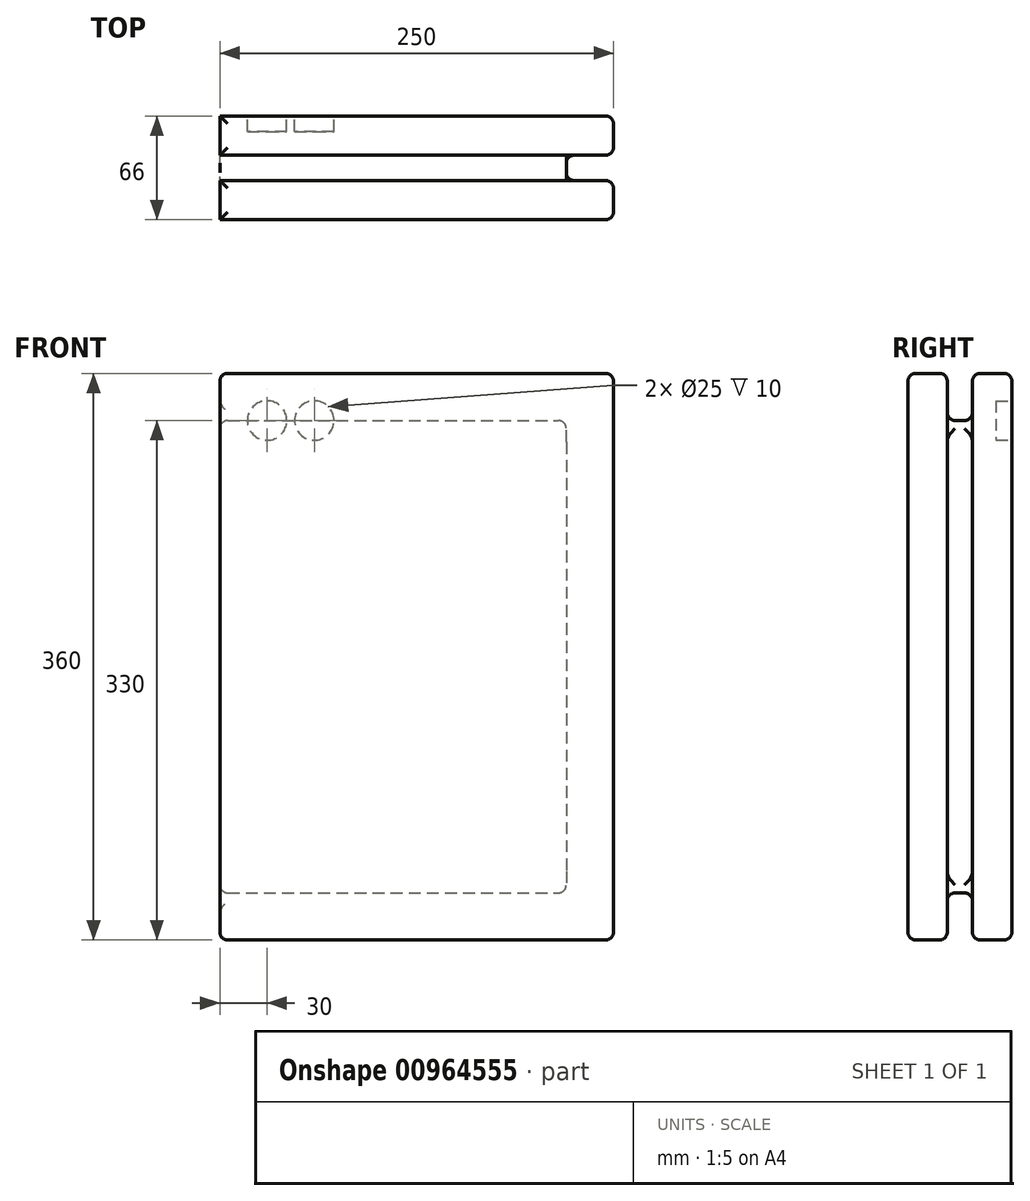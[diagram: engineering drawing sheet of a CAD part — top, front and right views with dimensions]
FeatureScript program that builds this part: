
annotation { "Feature Type Name" : "Feature", "Feature Type Description" : "" }
export const myFeature = defineFeature(function(context is Context, id is Id, definition is map)
    precondition{}
    {
        {
            var Q0;
            Q0=qCreatedBy(makeId("Right.planeOp"),FACE);
            var sketch = newSketch(context, id + "F0", { "sketchPlane" : qUnion([Q0])});
            skLineSegment(sketch, "E0", {"start": v(0, 0) * mm, "end": v(0, 150) * mm, "construction": true});
            skLineSegment(sketch, "E1", {"start": v(0, 0) * mm, "end": v(0, -150) * mm, "construction": true});
            skLineSegment(sketch, "E2", {"start": v(0, 150) * mm, "end": v(8, 150) * mm});
            skLineSegment(sketch, "E3", {"start": v(8, 150) * mm, "end": v(8, 180) * mm});
            skLineSegment(sketch, "E4", {"start": v(8, 180) * mm, "end": v(33, 180) * mm});
            skLineSegment(sketch, "E5", {"start": v(0, 0) * mm, "end": v(80, 0) * mm, "construction": true});
            skLineSegment(sketch, "E6", {"start": v(0, 0) * mm, "end": v(-80, 0) * mm, "construction": true});
            skLineSegment(sketch, "E7.MirrorCS", {"start": v(8, -180) * mm, "end": v(33, -180) * mm});
            skLineSegment(sketch, "E8.MirrorCS", {"start": v(8, -150) * mm, "end": v(8, -180) * mm});
            skLineSegment(sketch, "E9.MirrorCS", {"start": v(0, -150) * mm, "end": v(8, -150) * mm});
            skLineSegment(sketch, "E10", {"start": v(33, 180) * mm, "end": v(33, -180) * mm});
            skLineSegment(sketch, "E11", {"start": v(0, 150) * mm, "end": v(0, -150) * mm, "construction": true});
            skLineSegment(sketch, "E12.MirrorCS", {"start": v(0, 150) * mm, "end": v(-8, 150) * mm});
            skLineSegment(sketch, "E13.MirrorCS", {"start": v(-8, 150) * mm, "end": v(-8, 180) * mm});
            skLineSegment(sketch, "E14.MirrorCS", {"start": v(-8, 180) * mm, "end": v(-33, 180) * mm});
            skLineSegment(sketch, "E15.MirrorCS", {"start": v(-33, 180) * mm, "end": v(-33, -180) * mm});
            skLineSegment(sketch, "E16.MirrorCS", {"start": v(-8, -180) * mm, "end": v(-33, -180) * mm});
            skLineSegment(sketch, "E17.MirrorCS", {"start": v(-8, -150) * mm, "end": v(-8, -180) * mm});
            skLineSegment(sketch, "E18.MirrorCS", {"start": v(0, -150) * mm, "end": v(-8, -150) * mm});
            skSolve(sketch);
        }
        {
            var Q0;
            Q0=qCreatedBy(makeId("Front.planeOp"),FACE);
            var sketch = newSketch(context, id + "F1", { "sketchPlane" : qUnion([Q0])});
            skLineSegment(sketch, "E19", {"start": v(0, 0) * mm, "end": v(250, 0) * mm});
            skSolve(sketch);
        }
        {
            var Q0;
            Q0=qSketchRegion(id+"F0",true);
            var Q1;
            Q1=qConstructionFilter(qBodyType(qCreatedBy(id+"F1",EDGE),BodyType.WIRE),ConstructionObject.NO);
            sweep(context, id + "F2", {"profiles" : qUnion([Q0]), "path" : qUnion([Q1])});
        }
        {
            var Q0;
            Q0=makeQuery(id+"F2.opSweep","SWEPT_FACE",FACE,{"disambiguationData":[OSD([sQuery(id+"F0.wireOp",EDGE,"E10"),sQuery(id+"F1.wireOp",EDGE,"E19")])]});
            var sketch = newSketch(context, id + "F3", { "sketchPlane" : qUnion([Q0])});
            skLineSegment(sketch, "E20", {"start": v(0, 180) * mm, "end": v(-30, 180) * mm, "construction": true});
            skLineSegment(sketch, "E21", {"start": v(-30, 180) * mm, "end": v(-60, 180) * mm, "construction": true});
            skLineSegment(sketch, "E22", {"start": v(-30, 180) * mm, "end": v(-30, 150) * mm, "construction": true});
            skLineSegment(sketch, "E23", {"start": v(-60, 180) * mm, "end": v(-60, 150) * mm, "construction": true});
            skCircle(sketch, "E24", {"center": v(-30, 150) * mm, "radius": 12.5 * mm});
            skCircle(sketch, "E25", {"center": v(-60, 150) * mm, "radius": 12.5 * mm});
            skSolve(sketch);
        }
        {
            var Q0;
            Q0=makeQuery(id+"F3.imprint","IMPRINT",FACE,{"disambiguationData":[TD([[makeQuery(id+"F3.imprint","IMPRINT",EDGE,{"derivedFrom":sQuery(id+"F3.wireOp",EDGE,"E25")}),1.0]])]});
            var Q1;
            Q1=makeQuery(id+"F3.imprint","IMPRINT",FACE,{"disambiguationData":[TD([[makeQuery(id+"F3.imprint","IMPRINT",EDGE,{"derivedFrom":sQuery(id+"F3.wireOp",EDGE,"E24")}),1.0]])]});
            extrude(context, id + "F4", {"entities" : qUnion([Q0, Q1]), "operationType" : NewBodyOperationType.REMOVE, "oppositeDirection" : true, "depth" : 10 * mm, "offsetDistance" : 25 * mm});
        }
        {
            var Q0;
            Q0=makeQuery(id+"F2.opSweep","CAP_FACE",FACE,{"disambiguationData":[OSD([sQuery(id+"F0.wireOp",EDGE,"E2"),sQuery(id+"F0.wireOp",EDGE,"E3"),sQuery(id+"F0.wireOp",EDGE,"E4"),sQuery(id+"F0.wireOp",EDGE,"E7.MirrorCS"),sQuery(id+"F0.wireOp",EDGE,"E8.MirrorCS"),sQuery(id+"F0.wireOp",EDGE,"E9.MirrorCS"),sQuery(id+"F0.wireOp",EDGE,"E10"),sQuery(id+"F0.wireOp",EDGE,"E12.MirrorCS"),sQuery(id+"F0.wireOp",EDGE,"E13.MirrorCS"),sQuery(id+"F0.wireOp",EDGE,"E14.MirrorCS"),sQuery(id+"F0.wireOp",EDGE,"E15.MirrorCS"),sQuery(id+"F0.wireOp",EDGE,"E16.MirrorCS"),sQuery(id+"F0.wireOp",EDGE,"E17.MirrorCS"),sQuery(id+"F0.wireOp",EDGE,"E18.MirrorCS"),sQuery(id+"F1.wireOp",VERTEX,"E19.end")])],"isStart":false});
            var sketch = newSketch(context, id + "F5", { "sketchPlane" : qUnion([Q0])});
            skPoint(sketch, "E26", {"position": v(0, 0) * mm});
            skLineSegment(sketch, "E27", {"start": v(0, 0) * mm, "end": v(0, 150) * mm, "construction": true});
            skLineSegment(sketch, "E28", {"start": v(0, 0) * mm, "end": v(0, -150) * mm, "construction": true});
            skLineSegment(sketch, "E29", {"start": v(0, 150) * mm, "end": v(-8, 150) * mm});
            skLineSegment(sketch, "E30", {"start": v(-8, 150) * mm, "end": v(-8, -150) * mm});
            skLineSegment(sketch, "E31", {"start": v(-8, -150) * mm, "end": v(0, -150) * mm});
            skLineSegment(sketch, "E32.MirrorCS", {"start": v(0, 150) * mm, "end": v(8, 150) * mm});
            skLineSegment(sketch, "E33.MirrorCS", {"start": v(8, 150) * mm, "end": v(8, -150) * mm});
            skLineSegment(sketch, "E34.MirrorCS", {"start": v(8, -150) * mm, "end": v(0, -150) * mm});
            skSolve(sketch);
        }
        {
            var Q0;
            Q0=makeQuery(id+"F5.imprint","IMPRINT",FACE,{"disambiguationData":[TD([[makeQuery(id+"F5.imprint","IMPRINT",EDGE,{"derivedFrom":sQuery(id+"F5.wireOp",EDGE,"E29")}),1.0]])]});
            extrude(context, id + "F6", {"entities" : qUnion([Q0]), "operationType" : NewBodyOperationType.REMOVE, "oppositeDirection" : true, "depth" : 30 * mm, "offsetDistance" : 25 * mm});
        }
        {
            var Q0;
            Q0=makeQuery(id+"F2.opSweep","SWEPT_FACE",FACE,{"disambiguationData":[OSD([sQuery(id+"F0.wireOp",EDGE,"E2"),sQuery(id+"F0.wireOp",EDGE,"E12.MirrorCS"),sQuery(id+"F1.wireOp",EDGE,"E19")])]});
            var Q1;
            Q1=makeQuery(id+"F2.opSweep","SWEPT_FACE",FACE,{"disambiguationData":[OSD([sQuery(id+"F0.wireOp",EDGE,"E9.MirrorCS"),sQuery(id+"F0.wireOp",EDGE,"E18.MirrorCS"),sQuery(id+"F1.wireOp",EDGE,"E19")])]});
            var Q2;
            Q2=makeQuery(id+"F2.opSweep","SWEPT_FACE",FACE,{"disambiguationData":[OSD([sQuery(id+"F0.wireOp",EDGE,"E7.MirrorCS"),sQuery(id+"F1.wireOp",EDGE,"E19")])]});
            var Q3;
            {var subQ1=sQuery(id+"F0.wireOp",EDGE,"E8.MirrorCS");var subQ2=sQuery(id+"F0.wireOp",EDGE,"E7.MirrorCS");var subQ3=sQuery(id+"F0.wireOp",EDGE,"E4");var subQ4=sQuery(id+"F0.wireOp",EDGE,"E3");var subQ5=sQuery(id+"F0.wireOp",EDGE,"E10");Q3=makeQuery(id+"F6.boolean.opBoolean","SPLIT",FACE,{"disambiguationData":[TD([makeQuery(id+"F6.opExtrude","SWEPT_FACE",FACE,{"disambiguationData":[OSD([sQuery(id+"F5.wireOp",EDGE,"E33.MirrorCS")])]})])],"derivedFrom":makeQuery(id+"F2.opSweep","CAP_FACE",FACE,{"disambiguationData":[OSD([sQuery(id+"F0.wireOp",EDGE,"E2"),subQ4,subQ3,subQ2,subQ1,sQuery(id+"F0.wireOp",EDGE,"E9.MirrorCS"),subQ5,sQuery(id+"F0.wireOp",EDGE,"E12.MirrorCS"),sQuery(id+"F0.wireOp",EDGE,"E13.MirrorCS"),sQuery(id+"F0.wireOp",EDGE,"E14.MirrorCS"),sQuery(id+"F0.wireOp",EDGE,"E15.MirrorCS"),sQuery(id+"F0.wireOp",EDGE,"E16.MirrorCS"),sQuery(id+"F0.wireOp",EDGE,"E17.MirrorCS"),sQuery(id+"F0.wireOp",EDGE,"E18.MirrorCS"),sQuery(id+"F1.wireOp",VERTEX,"E19.end")])],"isStart":false})});}
            var Q4;
            Q4=makeQuery(id+"F2.opSweep","SWEPT_FACE",FACE,{"disambiguationData":[OSD([sQuery(id+"F0.wireOp",EDGE,"E4"),sQuery(id+"F1.wireOp",EDGE,"E19")])]});
            var Q5;
            Q5=makeQuery(id+"F2.opSweep","SWEPT_FACE",FACE,{"disambiguationData":[OSD([sQuery(id+"F0.wireOp",EDGE,"E14.MirrorCS"),sQuery(id+"F1.wireOp",EDGE,"E19")])]});
            var Q6;
            {var subQ1=sQuery(id+"F0.wireOp",EDGE,"E16.MirrorCS");var subQ2=sQuery(id+"F0.wireOp",EDGE,"E15.MirrorCS");var subQ3=sQuery(id+"F0.wireOp",EDGE,"E14.MirrorCS");var subQ4=sQuery(id+"F0.wireOp",EDGE,"E13.MirrorCS");var subQ5=sQuery(id+"F0.wireOp",EDGE,"E17.MirrorCS");Q6=makeQuery(id+"F6.boolean.opBoolean","SPLIT",FACE,{"disambiguationData":[TD([makeQuery(id+"F6.opExtrude","SWEPT_FACE",FACE,{"disambiguationData":[OSD([sQuery(id+"F5.wireOp",EDGE,"E30")])]})])],"derivedFrom":makeQuery(id+"F2.opSweep","CAP_FACE",FACE,{"disambiguationData":[OSD([sQuery(id+"F0.wireOp",EDGE,"E2"),sQuery(id+"F0.wireOp",EDGE,"E3"),sQuery(id+"F0.wireOp",EDGE,"E4"),sQuery(id+"F0.wireOp",EDGE,"E7.MirrorCS"),sQuery(id+"F0.wireOp",EDGE,"E8.MirrorCS"),sQuery(id+"F0.wireOp",EDGE,"E9.MirrorCS"),sQuery(id+"F0.wireOp",EDGE,"E10"),sQuery(id+"F0.wireOp",EDGE,"E12.MirrorCS"),subQ4,subQ3,subQ2,subQ1,subQ5,sQuery(id+"F0.wireOp",EDGE,"E18.MirrorCS"),sQuery(id+"F1.wireOp",VERTEX,"E19.end")])],"isStart":false})});}
            var Q7;
            Q7=makeQuery(id+"F2.opSweep","SWEPT_FACE",FACE,{"disambiguationData":[OSD([sQuery(id+"F0.wireOp",EDGE,"E16.MirrorCS"),sQuery(id+"F1.wireOp",EDGE,"E19")])]});
            fillet(context, id + "F7", {"entities" : qUnion([Q0, Q1, Q2, Q3, Q4, Q5, Q6, Q7]), "radius" : 5 * mm, "tangentPropagation" : true, "allowEdgeOverflow" : false});
        }
    });
